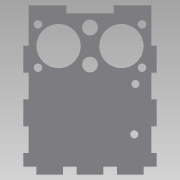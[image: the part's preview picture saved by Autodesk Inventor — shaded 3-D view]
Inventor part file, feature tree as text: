
AUTODESK INVENTOR PART (.ipt)
format: ipt  version: 2015 SP1 (Build 190203100, 203)  size: 228,864 bytes
history: native  units: mm
features: extrude x4, sketch x4
ambient origin geometry x8: Origin, YZ Plane, XZ Plane, XY Plane, X Axis, Y Axis, Z Axis, Center Point
bodies: Body1 (feature_tree)
feature tree (8):
  extrude  "Extrusion2"  Depth=3.0mm
  extrude  "Extrusion3"  Depth=3.0mm
  extrude  "Extrusion4"  Depth=3.0mm
  extrude  "Extrusion5"  Depth=3.0mm TaperAngle=0.0deg
  sketch  "Sketch1"  dims[d0=10.0mm d1=3.0mm]
  sketch  "Sketch2"  dims[d2=20.0mm d4=15.0mm d5=20.0mm d7=15.0mm d13=3.0mm]
  sketch  "Sketch3"  dims[d14=180.0deg d15=3.0mm]
  sketch  "Sketch4"  dims[d17=7.675mm d18=7.675mm d21=3.0mm d22=0.0mm d23=2.999814mm d24=1.0mm d25=1.0mm d26=3.0mm d27=0.0mm d28=1.0mm d29=1.0mm d30=11.700171mm d31=11.699829mm d32=7.675mm d33=7.675mm d34=11.699829mm d35=11.700171mm d45=8.061mm d46=8.061mm d47=2.0mm d48=2.0mm d49=3.0mm d50=0.0mm d51=3.0mm d52=0.0mm]
